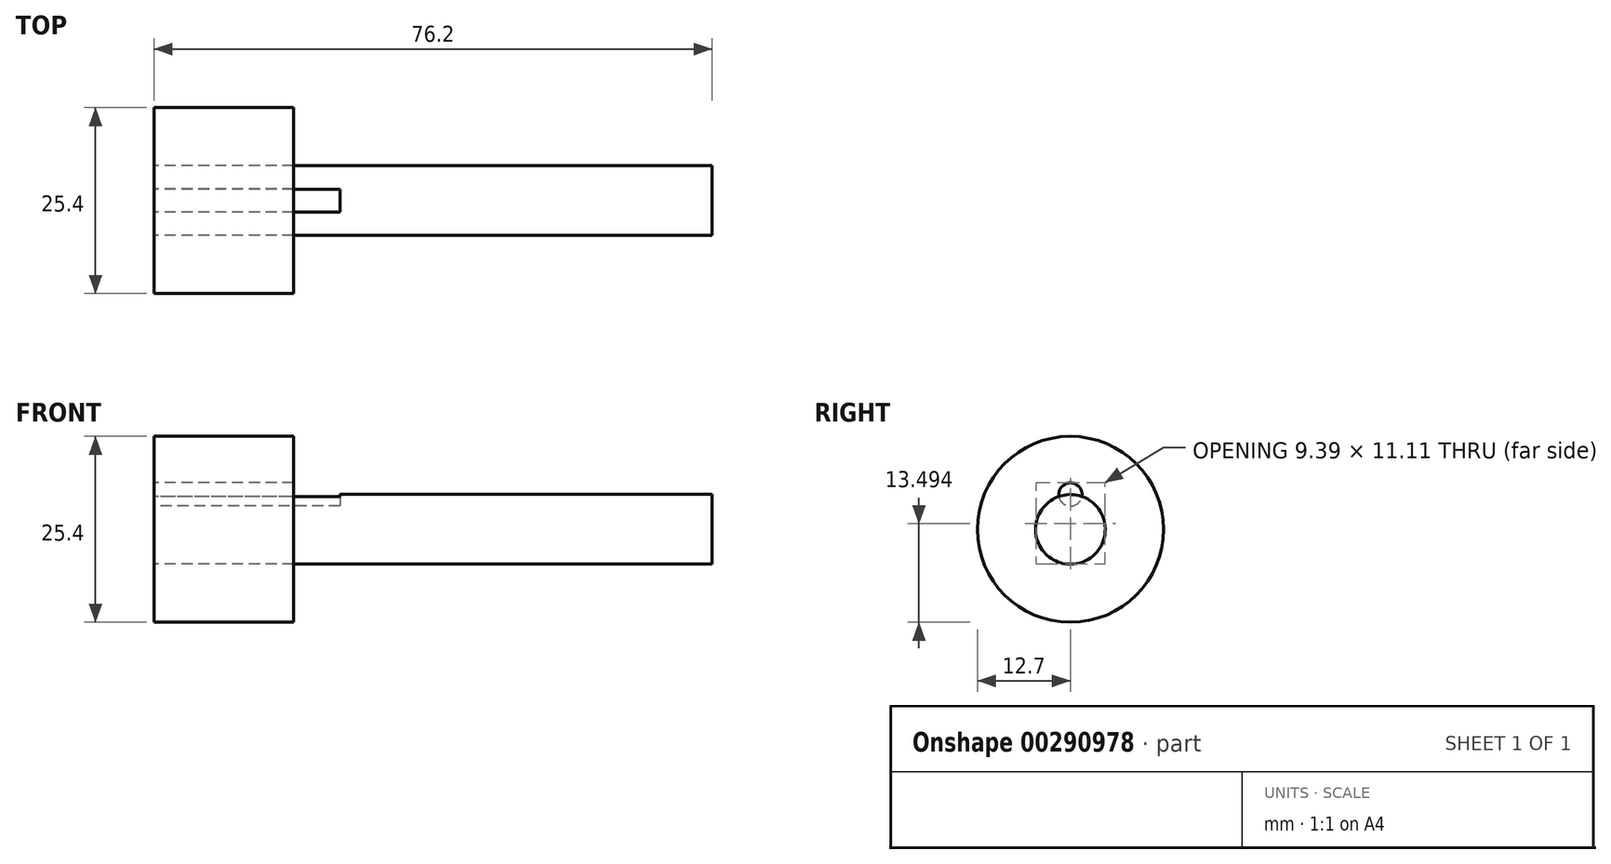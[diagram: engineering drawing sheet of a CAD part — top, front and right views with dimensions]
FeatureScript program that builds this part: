
annotation { "Feature Type Name" : "Feature", "Feature Type Description" : "" }
export const myFeature = defineFeature(function(context is Context, id is Id, definition is map)
    precondition{}
    {
        {
            var Q0;
            Q0=qCreatedBy(makeId("Right.planeOp"),FACE);
            var sketch = newSketch(context, id + "F0", { "sketchPlane" : qUnion([Q0])});
            skCircle(sketch, "E0", {"center": v(0, 0) * mm, "radius": 4.76 * mm});
            skSolve(sketch);
        }
        {
            var Q0;
            Q0 = qSketchRegion(id + "F0", true);
            extrude(context, id + "F1", {"entities" : qUnion([Q0]), "depth" : 76.2 * mm});
        }
        {
            var Q0;
            Q0=qCreatedBy(makeId("Right.planeOp"),FACE);
            var sketch = newSketch(context, id + "F2", { "sketchPlane" : qUnion([Q0])});
            skCircle(sketch, "E1", {"center": v(0, 4.76) * mm, "radius": 1.59 * mm});
            skSolve(sketch);
        }
        {
            var Q0;
            Q0=makeQuery(id+"F1.opExtrude","CAP_FACE",FACE,{"disambiguationData":[OSD([sQuery(id+"F0.wireOp",EDGE,"E0")])],"isStart":true});
            var sketch = newSketch(context, id + "F3", { "sketchPlane" : qUnion([Q0])});
            skCircle(sketch, "E2", {"center": v(0, 0) * mm, "radius": 12.7 * mm});
            skSolve(sketch);
        }
        {
            var Q0;
            Q0=makeQuery(id+"F3.imprint","IMPRINT",FACE,{"disambiguationData":[TD([[makeQuery(id+"F3.imprint","IMPRINT",EDGE,{"derivedFrom":sQuery(id+"F3.wireOp",EDGE,"E2")}),1.0]])]});
            extrude(context, id + "F4", {"entities" : qUnion([Q0]), "oppositeDirection" : true, "depth" : 19.05 * mm});
        }
        {
            var Q0;
            Q0=makeQuery(id+"F2.imprint","IMPRINT",FACE,{"disambiguationData":[TD([[makeQuery(id+"F2.imprint","IMPRINT",EDGE,{"derivedFrom":sQuery(id+"F2.wireOp",EDGE,"E1")}),1.0]])]});
            extrude(context, id + "F5", {"entities" : qUnion([Q0]), "operationType" : NewBodyOperationType.REMOVE, "depth" : 25.4 * mm});
        }
    });
